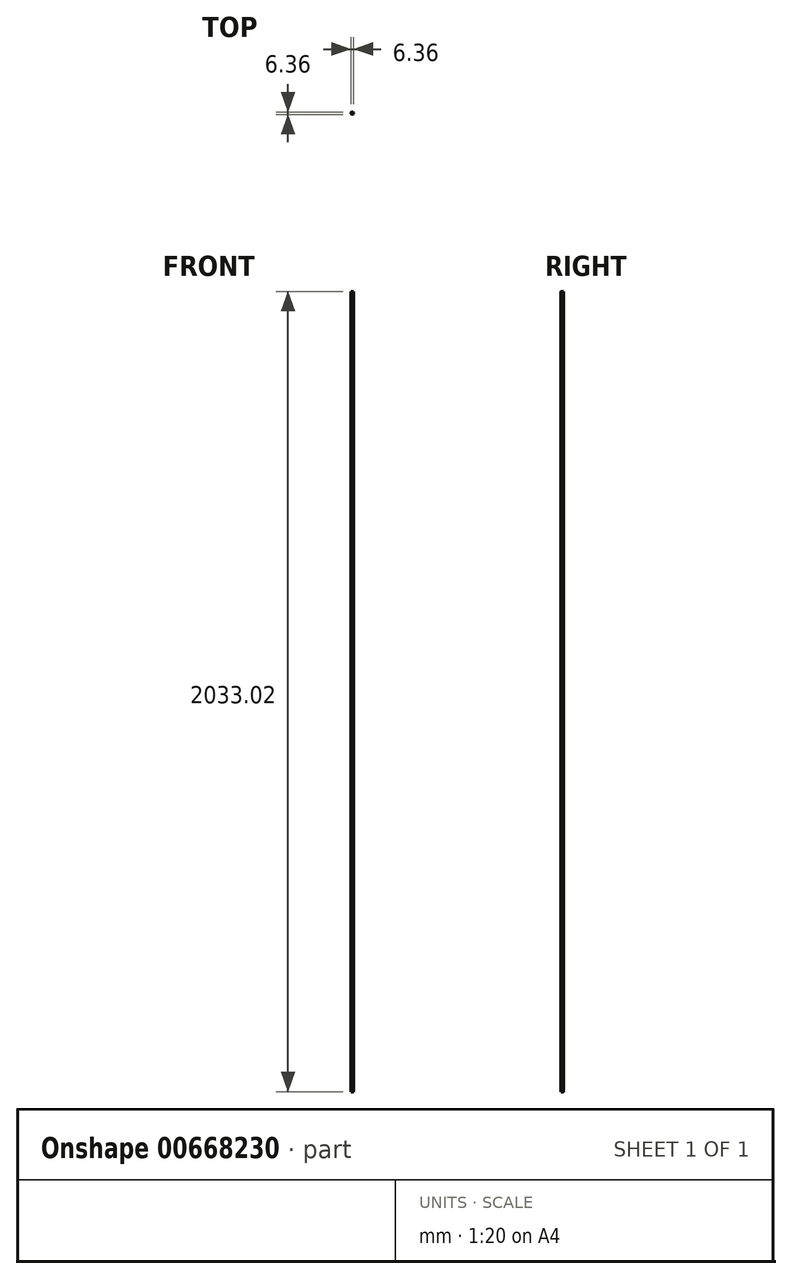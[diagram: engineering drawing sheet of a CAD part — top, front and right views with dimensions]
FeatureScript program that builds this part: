
annotation { "Feature Type Name" : "Feature", "Feature Type Description" : "" }
export const myFeature = defineFeature(function(context is Context, id is Id, definition is map)
    precondition{}
    {
        {
            var Q0;
            Q0=qCreatedBy(makeId("Top.planeOp"),FACE);
            var sketch = newSketch(context, id + "F0", { "sketchPlane" : qUnion([Q0])});
            skCircle(sketch, "E0", {"center": v(0, 0) * mm, "radius": 3.18 * mm});
            skSolve(sketch);
        }
        {
            var Q0;
            Q0=makeQuery(id+"F0.imprint","IMPRINT",FACE,{"disambiguationData":[TD([[makeQuery(id+"F0.imprint","IMPRINT",EDGE,{"derivedFrom":sQuery(id+"F0.wireOp",EDGE,"E0")}),1.0]])]});
            extrude(context, id + "F1", {"entities" : qUnion([Q0]), "depth" : 2033.02 * mm, "offsetDistance" : 25.4 * mm});
        }
    });
